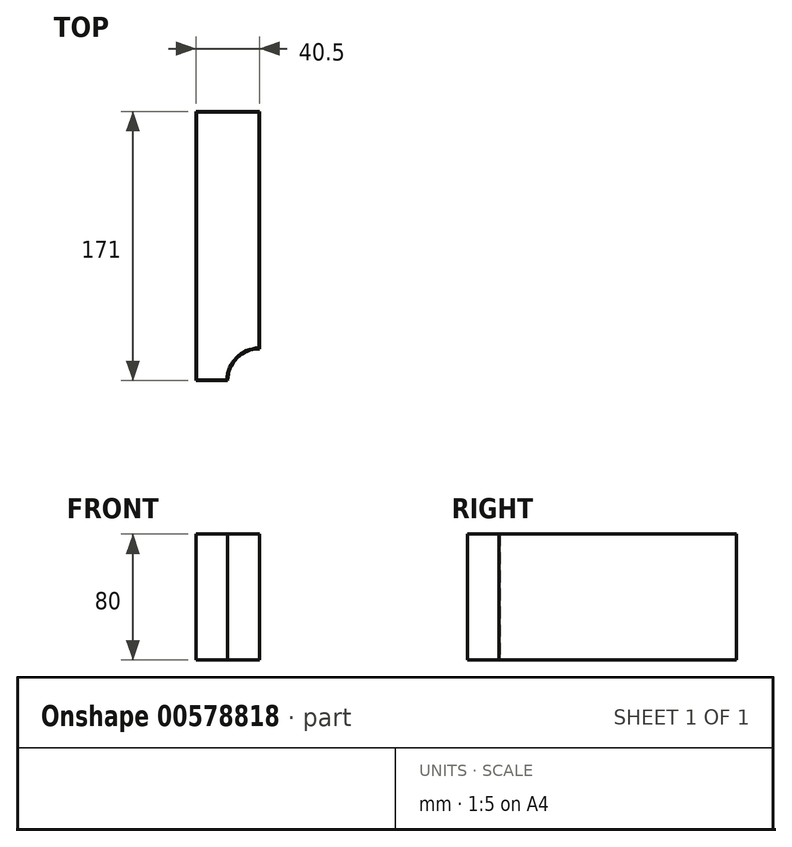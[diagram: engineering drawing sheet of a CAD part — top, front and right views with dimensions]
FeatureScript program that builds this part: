
annotation { "Feature Type Name" : "Feature", "Feature Type Description" : "" }
export const myFeature = defineFeature(function(context is Context, id is Id, definition is map)
    precondition{}
    {
        {
            var Q0;
            Q0=qCreatedBy(makeId("Top.planeOp"),FACE);
            var sketch = newSketch(context, id + "F0", { "sketchPlane" : qUnion([Q0])});
            skLineSegment(sketch, "E0.bottom", {"start": v(-19.28, 122.28) * mm, "end": v(21.22, 122.28) * mm});
            skLineSegment(sketch, "E0.top", {"start": v(-19.28, -48.72) * mm, "end": v(0.97, -48.72) * mm});
            skLineSegment(sketch, "E0.left", {"start": v(-19.28, 122.28) * mm, "end": v(-19.28, -48.72) * mm});
            skLineSegment(sketch, "E0.right", {"start": v(21.22, 122.28) * mm, "end": v(21.22, -28.47) * mm});
            skArc(sketch, "E1", {"start": v(0.97, -48.72) * mm, "mid": v(6.9, -34.4) * mm, "end": v(21.22, -28.47) * mm});
            skSolve(sketch);
        }
        {
            var Q0;
            Q0=makeQuery(id+"F0.imprint","IMPRINT",FACE,{"disambiguationData":[TD([[makeQuery(id+"F0.imprint","IMPRINT",EDGE,{"derivedFrom":sQuery(id+"F0.wireOp",EDGE,"E0.bottom")}),-1.0]])]});
            extrude(context, id + "F1", {"entities" : qUnion([Q0]), "depth" : 80 * mm, "offsetDistance" : 25 * mm});
        }
        {
            var Q0;
            Q0=makeQuery(id+"F1.opExtrude","CAP_FACE",FACE,{"disambiguationData":[OSD([sQuery(id+"F0.wireOp",EDGE,"E0.bottom"),sQuery(id+"F0.wireOp",EDGE,"E0.top"),sQuery(id+"F0.wireOp",EDGE,"E0.left"),sQuery(id+"F0.wireOp",EDGE,"E0.right"),sQuery(id+"F0.wireOp",EDGE,"E1")])],"isStart":false});
            shell(context, id + "F2", {"entities" : qUnion([Q0]), "thickness" : 0.5 * mm});
        }
    });
